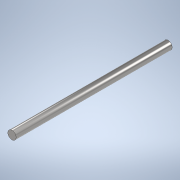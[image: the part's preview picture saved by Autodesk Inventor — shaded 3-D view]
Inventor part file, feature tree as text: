
AUTODESK INVENTOR PART (.ipt)
format: ipt  version: 2020 (Build 240168000, 168)  size: 93,696 bytes
history: native  units: mm
features: extrude x1, sketch x1
ambient origin geometry x8: Origin, YZ Plane, XZ Plane, XY Plane, X Axis, Y Axis, Z Axis, Center Point
bodies: Solid1 (feature_tree)
feature tree (2):
  extrude  "Extrusion1"  Depth=150.0mm TaperAngle=0.0deg
  sketch  "Sketch1"  dims[d0=8.0mm d1=150.0mm d2=0.0mm]
